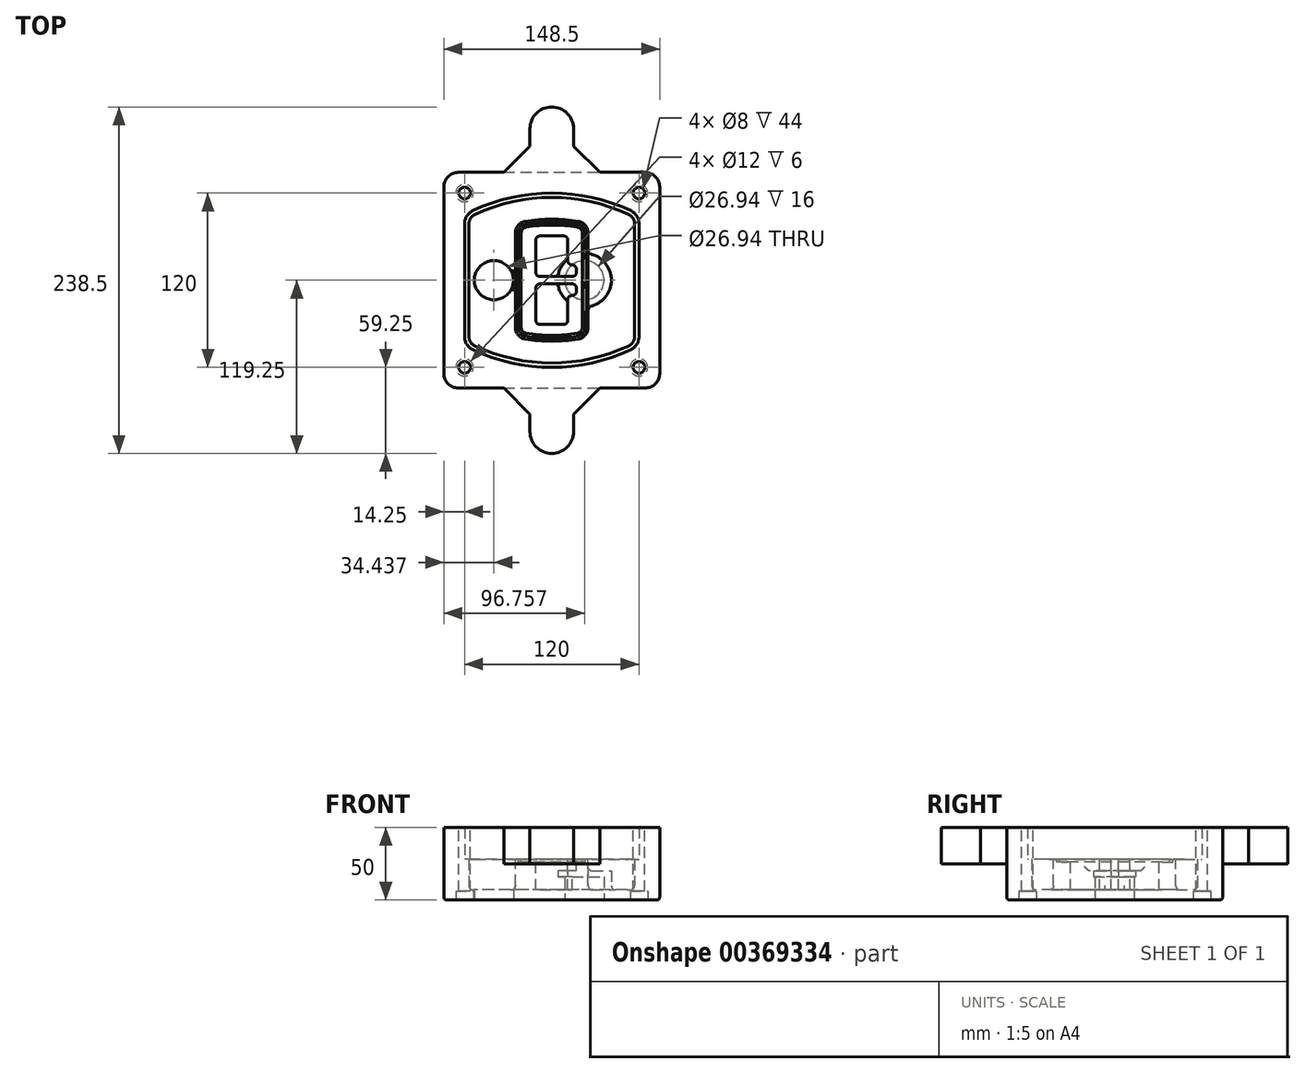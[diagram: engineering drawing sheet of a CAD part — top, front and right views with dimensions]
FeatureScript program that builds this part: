
annotation { "Feature Type Name" : "Feature", "Feature Type Description" : "" }
export const myFeature = defineFeature(function(context is Context, id is Id, definition is map)
    precondition{}
    {
        {
            var Q0;
            Q0=qCreatedBy(makeId("Top.planeOp"),FACE);
            var sketch = newSketch(context, id + "F0", { "sketchPlane" : qUnion([Q0])});
            skPoint(sketch, "E0.rect.middle", {"position": v(0, 0) * mm});
            skLineSegment(sketch, "E1.bottom", {"start": v(-64.25, -74.25) * mm, "end": v(64.25, -74.25) * mm});
            skLineSegment(sketch, "E1.top", {"start": v(-64.25, 74.25) * mm, "end": v(64.25, 74.25) * mm});
            skLineSegment(sketch, "E1.left", {"start": v(-74.25, -64.25) * mm, "end": v(-74.25, 64.25) * mm});
            skLineSegment(sketch, "E1.right", {"start": v(74.25, -64.25) * mm, "end": v(74.25, 64.25) * mm});
            skLineSegment(sketch, "E2", {"start": v(-74.25, 74.25) * mm, "end": v(74.25, -74.25) * mm, "construction": true});
            skLineSegment(sketch, "E3", {"start": v(74.25, 74.25) * mm, "end": v(-74.25, -74.25) * mm, "construction": true});
            skCircle(sketch, "E4", {"center": v(-60, 60) * mm, "radius": 4 * mm});
            skCircle(sketch, "E5", {"center": v(60, 60) * mm, "radius": 4 * mm});
            skCircle(sketch, "E6", {"center": v(60, -60) * mm, "radius": 4 * mm});
            skCircle(sketch, "E7", {"center": v(-60, -60) * mm, "radius": 4 * mm});
            skLineSegment(sketch, "E8", {"start": v(-60, 60) * mm, "end": v(60, 60) * mm, "construction": true});
            skLineSegment(sketch, "E9", {"start": v(60, 60) * mm, "end": v(60, -60) * mm, "construction": true});
            skLineSegment(sketch, "E10", {"start": v(60, -60) * mm, "end": v(-60, -60) * mm, "construction": true});
            skLineSegment(sketch, "E11", {"start": v(-60, -60) * mm, "end": v(-60, 60) * mm, "construction": true});
            skLineSegment(sketch, "E12", {"start": v(-60, 38.83) * mm, "end": v(-60, -38.83) * mm});
            skLineSegment(sketch, "E13", {"start": v(60, 38.83) * mm, "end": v(60, -38.83) * mm});
            skArc(sketch, "E14", {"start": v(54.26, 47.88) * mm, "mid": v(0, 60) * mm, "end": v(-54.26, 47.88) * mm});
            skArc(sketch, "E15", {"start": v(-54.26, -47.88) * mm, "mid": v(0, -60) * mm, "end": v(54.26, -47.88) * mm});
            skLineSegment(sketch, "E16", {"start": v(-60, 0) * mm, "end": v(60, 0) * mm, "construction": true});
            skPoint(sketch, "E17.visualSharp", {"position": v(-60, -45) * mm});
            skArc(sketch, "E17.filletArc", {"start": v(-60, -38.83) * mm, "mid": v(-58.44, -44.2) * mm, "end": v(-54.26, -47.88) * mm});
            skPoint(sketch, "E18.visualSharp", {"position": v(-60, 45) * mm});
            skArc(sketch, "E18.filletArc", {"start": v(-54.26, 47.88) * mm, "mid": v(-58.44, 44.2) * mm, "end": v(-60, 38.83) * mm});
            skPoint(sketch, "E19.visualSharp", {"position": v(60, 45) * mm});
            skArc(sketch, "E19.filletArc", {"start": v(60, 38.83) * mm, "mid": v(58.44, 44.2) * mm, "end": v(54.26, 47.88) * mm});
            skPoint(sketch, "E20.visualSharp", {"position": v(60, -45) * mm});
            skArc(sketch, "E20.filletArc", {"start": v(54.26, -47.88) * mm, "mid": v(58.44, -44.2) * mm, "end": v(60, -38.83) * mm});
            skPoint(sketch, "E21.visualSharp", {"position": v(-74.25, 74.25) * mm});
            skArc(sketch, "E21.filletArc", {"start": v(-64.25, 74.25) * mm, "mid": v(-71.32, 71.32) * mm, "end": v(-74.25, 64.25) * mm});
            skPoint(sketch, "E22.visualSharp", {"position": v(74.25, 74.25) * mm});
            skArc(sketch, "E22.filletArc", {"start": v(74.25, 64.25) * mm, "mid": v(71.32, 71.32) * mm, "end": v(64.25, 74.25) * mm});
            skPoint(sketch, "E23.visualSharp", {"position": v(74.25, -74.25) * mm});
            skArc(sketch, "E23.filletArc", {"start": v(64.25, -74.25) * mm, "mid": v(71.32, -71.32) * mm, "end": v(74.25, -64.25) * mm});
            skPoint(sketch, "E24.visualSharp", {"position": v(-74.25, -74.25) * mm});
            skArc(sketch, "E24.filletArc", {"start": v(-74.25, -64.25) * mm, "mid": v(-71.32, -71.32) * mm, "end": v(-64.25, -74.25) * mm});
            skArc(sketch, "E25.0", {"start": v(57, 38.83) * mm, "mid": v(55.9, 42.58) * mm, "end": v(52.98, 45.17) * mm});
            skLineSegment(sketch, "E25.1", {"start": v(57, 38.83) * mm, "end": v(57, -38.83) * mm});
            skArc(sketch, "E25.2", {"start": v(52.98, -45.17) * mm, "mid": v(55.9, -42.58) * mm, "end": v(57, -38.83) * mm});
            skArc(sketch, "E25.3", {"start": v(-52.98, -45.17) * mm, "mid": v(0, -57) * mm, "end": v(52.98, -45.17) * mm});
            skArc(sketch, "E25.4", {"start": v(-57, -38.83) * mm, "mid": v(-55.9, -42.58) * mm, "end": v(-52.98, -45.17) * mm});
            skArc(sketch, "E25.5", {"start": v(52.98, 45.17) * mm, "mid": v(0, 57) * mm, "end": v(-52.98, 45.17) * mm});
            skLineSegment(sketch, "E25.6", {"start": v(-57, 38.83) * mm, "end": v(-57, -38.83) * mm});
            skArc(sketch, "E25.7", {"start": v(-52.98, 45.17) * mm, "mid": v(-55.9, 42.58) * mm, "end": v(-57, 38.83) * mm});
            skArc(sketch, "E26.0", {"start": v(-55.96, 51.5) * mm, "mid": v(-61.82, 46.33) * mm, "end": v(-64, 38.83) * mm});
            skArc(sketch, "E26.1", {"start": v(55.96, 51.5) * mm, "mid": v(0, 64) * mm, "end": v(-55.96, 51.5) * mm});
            skArc(sketch, "E26.2", {"start": v(64, 38.83) * mm, "mid": v(61.82, 46.33) * mm, "end": v(55.96, 51.5) * mm});
            skLineSegment(sketch, "E26.3", {"start": v(64, 38.83) * mm, "end": v(64, -38.83) * mm});
            skArc(sketch, "E26.4", {"start": v(55.96, -51.5) * mm, "mid": v(61.82, -46.33) * mm, "end": v(64, -38.83) * mm});
            skLineSegment(sketch, "E26.5", {"start": v(-64, 38.83) * mm, "end": v(-64, -38.83) * mm});
            skArc(sketch, "E26.6", {"start": v(-55.96, -51.5) * mm, "mid": v(0, -64) * mm, "end": v(55.96, -51.5) * mm});
            skArc(sketch, "E26.7", {"start": v(-64, -38.83) * mm, "mid": v(-61.82, -46.33) * mm, "end": v(-55.96, -51.5) * mm});
            skSolve(sketch);
        }
        {
            var Q0;
            Q0=makeQuery(id+"F0.imprint","IMPRINT",FACE,{"disambiguationData":[TD([[makeQuery(id+"F0.imprint","IMPRINT",EDGE,{"derivedFrom":sQuery(id+"F0.wireOp",EDGE,"E1.bottom")}),1.0]])]});
            var Q1;
            Q1=makeQuery(id+"F0.imprint","IMPRINT",FACE,{"disambiguationData":[TD([[makeQuery(id+"F0.imprint","IMPRINT",EDGE,{"derivedFrom":sQuery(id+"F0.wireOp",EDGE,"E12")}),1.0]])]});
            var Q2;
            Q2=makeQuery(id+"F0.imprint","IMPRINT",FACE,{"disambiguationData":[TD([[makeQuery(id+"F0.imprint","IMPRINT",EDGE,{"derivedFrom":sQuery(id+"F0.wireOp",EDGE,"E25.0")}),1.0]])]});
            var Q3;
            Q3=makeQuery(id+"F0.imprint","IMPRINT",FACE,{"disambiguationData":[TD([[makeQuery(id+"F0.imprint","IMPRINT",EDGE,{"derivedFrom":sQuery(id+"F0.wireOp",EDGE,"E12")}),-1.0]])]});
            extrude(context, id + "F1", {"entities" : qUnion([Q0, Q1, Q2, Q3]), "oppositeDirection" : true, "depth" : 25 * mm});
        }
        {
            var Q0;
            Q0=makeQuery(id+"F0.imprint","IMPRINT",FACE,{"disambiguationData":[TD([[makeQuery(id+"F0.imprint","IMPRINT",EDGE,{"derivedFrom":sQuery(id+"F0.wireOp",EDGE,"E12")}),1.0]])]});
            extrude(context, id + "F2", {"entities" : qUnion([Q0]), "operationType" : NewBodyOperationType.ADD, "depth" : 3 * mm});
        }
        {
            var Q0;
            Q0=makeQuery(id+"F0.imprint","IMPRINT",FACE,{"disambiguationData":[TD([[makeQuery(id+"F0.imprint","IMPRINT",EDGE,{"derivedFrom":sQuery(id+"F0.wireOp",EDGE,"E25.0")}),1.0]])]});
            extrude(context, id + "F3", {"entities" : qUnion([Q0]), "operationType" : NewBodyOperationType.REMOVE, "oppositeDirection" : true, "depth" : 18 * mm});
        }
        {
            var Q0;
            Q0=makeQuery(id+"F2.opExtrude","CAP_FACE",FACE,{"disambiguationData":[OSD([sQuery(id+"F0.wireOp",EDGE,"E12"),sQuery(id+"F0.wireOp",EDGE,"E13"),sQuery(id+"F0.wireOp",EDGE,"E14"),sQuery(id+"F0.wireOp",EDGE,"E15"),sQuery(id+"F0.wireOp",EDGE,"E17.filletArc"),sQuery(id+"F0.wireOp",EDGE,"E18.filletArc"),sQuery(id+"F0.wireOp",EDGE,"E19.filletArc"),sQuery(id+"F0.wireOp",EDGE,"E20.filletArc"),sQuery(id+"F0.wireOp",EDGE,"E25.0"),sQuery(id+"F0.wireOp",EDGE,"E25.1"),sQuery(id+"F0.wireOp",EDGE,"E25.2"),sQuery(id+"F0.wireOp",EDGE,"E25.3"),sQuery(id+"F0.wireOp",EDGE,"E25.4"),sQuery(id+"F0.wireOp",EDGE,"E25.5"),sQuery(id+"F0.wireOp",EDGE,"E25.6"),sQuery(id+"F0.wireOp",EDGE,"E25.7")])],"isStart":false});
            var sketch = newSketch(context, id + "F4", { "sketchPlane" : qUnion([Q0])});
            skArc(sketch, "E27.0", {"start": v(-18.34, -40.45) * mm, "mid": v(0, -42) * mm, "end": v(18.34, -40.45) * mm});
            skArc(sketch, "E28.0", {"start": v(18.34, 40.45) * mm, "mid": v(0, 42) * mm, "end": v(-18.34, 40.45) * mm});
            skLineSegment(sketch, "E29", {"start": v(-25, 32.57) * mm, "end": v(-25, -32.57) * mm});
            skLineSegment(sketch, "E30", {"start": v(25, 32.57) * mm, "end": v(25, -32.57) * mm});
            skLineSegment(sketch, "E31", {"start": v(-25, 39.1) * mm, "end": v(25, 39.1) * mm, "construction": true});
            skLineSegment(sketch, "E32", {"start": v(-25, -39.1) * mm, "end": v(25, -39.1) * mm, "construction": true});
            skPoint(sketch, "E33.visualSharp", {"position": v(-25, 39.1) * mm});
            skArc(sketch, "E33.filletArc", {"start": v(-18.34, 40.45) * mm, "mid": v(-23.11, 37.73) * mm, "end": v(-25, 32.57) * mm});
            skPoint(sketch, "E34.visualSharp", {"position": v(25, 39.1) * mm});
            skArc(sketch, "E34.filletArc", {"start": v(25, 32.57) * mm, "mid": v(23.11, 37.73) * mm, "end": v(18.34, 40.45) * mm});
            skPoint(sketch, "E35.visualSharp", {"position": v(25, -39.1) * mm});
            skArc(sketch, "E35.filletArc", {"start": v(18.34, -40.45) * mm, "mid": v(23.11, -37.73) * mm, "end": v(25, -32.57) * mm});
            skPoint(sketch, "E36.visualSharp", {"position": v(-25, -39.1) * mm});
            skArc(sketch, "E36.filletArc", {"start": v(-25, -32.57) * mm, "mid": v(-23.11, -37.73) * mm, "end": v(-18.34, -40.45) * mm});
            skArc(sketch, "E37.0", {"start": v(52.98, 45.17) * mm, "mid": v(0, 57) * mm, "end": v(-52.98, 45.17) * mm});
            skArc(sketch, "E37.1", {"start": v(-52.98, 45.17) * mm, "mid": v(-55.9, 42.58) * mm, "end": v(-57, 38.83) * mm});
            skLineSegment(sketch, "E37.2", {"start": v(-57, 38.83) * mm, "end": v(-57, -38.83) * mm});
            skArc(sketch, "E37.3", {"start": v(-57, -38.83) * mm, "mid": v(-55.9, -42.58) * mm, "end": v(-52.98, -45.17) * mm});
            skArc(sketch, "E37.4", {"start": v(-52.98, -45.17) * mm, "mid": v(0, -57) * mm, "end": v(52.98, -45.17) * mm});
            skArc(sketch, "E37.5", {"start": v(52.98, -45.17) * mm, "mid": v(55.9, -42.58) * mm, "end": v(57, -38.83) * mm});
            skLineSegment(sketch, "E37.6", {"start": v(57, 38.83) * mm, "end": v(57, -38.83) * mm});
            skArc(sketch, "E37.7", {"start": v(57, 38.83) * mm, "mid": v(55.9, 42.58) * mm, "end": v(52.98, 45.17) * mm});
            skLineSegment(sketch, "E38.0", {"start": v(23, 32.57) * mm, "end": v(23, -32.57) * mm});
            skArc(sketch, "E38.1", {"start": v(18, -38.48) * mm, "mid": v(21.58, -36.44) * mm, "end": v(23, -32.57) * mm});
            skArc(sketch, "E38.2", {"start": v(-18, -38.48) * mm, "mid": v(0, -40) * mm, "end": v(18, -38.48) * mm});
            skArc(sketch, "E38.3", {"start": v(-23, -32.57) * mm, "mid": v(-21.58, -36.44) * mm, "end": v(-18, -38.48) * mm});
            skLineSegment(sketch, "E38.4", {"start": v(-23, 32.57) * mm, "end": v(-23, -32.57) * mm});
            skArc(sketch, "E38.5", {"start": v(23, 32.57) * mm, "mid": v(21.58, 36.44) * mm, "end": v(18, 38.48) * mm});
            skArc(sketch, "E38.6", {"start": v(-18, 38.48) * mm, "mid": v(-21.58, 36.44) * mm, "end": v(-23, 32.57) * mm});
            skArc(sketch, "E38.7", {"start": v(18, 38.48) * mm, "mid": v(0, 40) * mm, "end": v(-18, 38.48) * mm});
            skArc(sketch, "E39.0", {"start": v(21, 32.57) * mm, "mid": v(20.06, 35.15) * mm, "end": v(17.67, 36.5) * mm});
            skLineSegment(sketch, "E39.1", {"start": v(21, 32.57) * mm, "end": v(21, -32.57) * mm});
            skArc(sketch, "E39.2", {"start": v(17.67, -36.5) * mm, "mid": v(20.06, -35.15) * mm, "end": v(21, -32.57) * mm});
            skArc(sketch, "E39.3", {"start": v(-17.67, -36.5) * mm, "mid": v(0, -38) * mm, "end": v(17.67, -36.5) * mm});
            skArc(sketch, "E39.4", {"start": v(-21, -32.57) * mm, "mid": v(-20.06, -35.15) * mm, "end": v(-17.67, -36.5) * mm});
            skArc(sketch, "E39.5", {"start": v(17.67, 36.5) * mm, "mid": v(0, 38) * mm, "end": v(-17.67, 36.5) * mm});
            skLineSegment(sketch, "E39.6", {"start": v(-21, 32.57) * mm, "end": v(-21, -32.57) * mm});
            skArc(sketch, "E39.7", {"start": v(-17.67, 36.5) * mm, "mid": v(-20.06, 35.15) * mm, "end": v(-21, 32.57) * mm});
            skLineSegment(sketch, "E40", {"start": v(-25, 0) * mm, "end": v(25, 0) * mm, "construction": true});
            skLineSegment(sketch, "E41", {"start": v(-11, 5.5) * mm, "end": v(-11, 27.5) * mm});
            skLineSegment(sketch, "E42", {"start": v(-8, 30.5) * mm, "end": v(8, 30.5) * mm});
            skLineSegment(sketch, "E43", {"start": v(11, 27.5) * mm, "end": v(11, 13.5) * mm});
            skLineSegment(sketch, "E44", {"start": v(14, 10.5) * mm, "end": v(14, 10.5) * mm});
            skLineSegment(sketch, "E45", {"start": v(17, 7.5) * mm, "end": v(17, 5.5) * mm});
            skLineSegment(sketch, "E46", {"start": v(14, 2.5) * mm, "end": v(-8, 2.5) * mm});
            skPoint(sketch, "E47.visualSharp", {"position": v(-11, 30.5) * mm});
            skArc(sketch, "E47.filletArc", {"start": v(-8, 30.5) * mm, "mid": v(-10.12, 29.62) * mm, "end": v(-11, 27.5) * mm});
            skPoint(sketch, "E48.visualSharp", {"position": v(11, 30.5) * mm});
            skArc(sketch, "E48.filletArc", {"start": v(11, 27.5) * mm, "mid": v(10.12, 29.62) * mm, "end": v(8, 30.5) * mm});
            skPoint(sketch, "E49.visualSharp", {"position": v(11, 10.5) * mm});
            skArc(sketch, "E49.filletArc", {"start": v(11, 13.5) * mm, "mid": v(11.88, 11.38) * mm, "end": v(14, 10.5) * mm});
            skPoint(sketch, "E50.visualSharp", {"position": v(17, 10.5) * mm});
            skArc(sketch, "E50.filletArc", {"start": v(17, 7.5) * mm, "mid": v(16.12, 9.62) * mm, "end": v(14, 10.5) * mm});
            skPoint(sketch, "E51.visualSharp", {"position": v(17, 2.5) * mm});
            skArc(sketch, "E51.filletArc", {"start": v(14, 2.5) * mm, "mid": v(16.12, 3.38) * mm, "end": v(17, 5.5) * mm});
            skPoint(sketch, "E52.visualSharp", {"position": v(-11, 2.5) * mm});
            skArc(sketch, "E52.filletArc", {"start": v(-11, 5.5) * mm, "mid": v(-10.12, 3.38) * mm, "end": v(-8, 2.5) * mm});
            skLineSegment(sketch, "E53.0.MirrorCS", {"start": v(14, -2.5) * mm, "end": v(-8, -2.5) * mm});
            skArc(sketch, "E54.0.MirrorCS", {"start": v(-11, -5.5) * mm, "mid": v(-10.12, -3.38) * mm, "end": v(-8, -2.5) * mm});
            skLineSegment(sketch, "E55.0.MirrorCS", {"start": v(-11, -5.5) * mm, "end": v(-11, -27.5) * mm});
            skArc(sketch, "E56.0.MirrorCS", {"start": v(-8, -30.5) * mm, "mid": v(-10.12, -29.62) * mm, "end": v(-11, -27.5) * mm});
            skLineSegment(sketch, "E57.0.MirrorCS", {"start": v(-8, -30.5) * mm, "end": v(8, -30.5) * mm});
            skArc(sketch, "E58.0.MirrorCS", {"start": v(11, -27.5) * mm, "mid": v(10.12, -29.62) * mm, "end": v(8, -30.5) * mm});
            skLineSegment(sketch, "E59.0.MirrorCS", {"start": v(11, -27.5) * mm, "end": v(11, -13.5) * mm});
            skArc(sketch, "E60.0.MirrorCS", {"start": v(11, -13.5) * mm, "mid": v(11.88, -11.38) * mm, "end": v(14, -10.5) * mm});
            skArc(sketch, "E61.0.MirrorCS", {"start": v(17, -7.5) * mm, "mid": v(16.12, -9.62) * mm, "end": v(14, -10.5) * mm});
            skLineSegment(sketch, "E62.0.MirrorCS", {"start": v(17, -7.5) * mm, "end": v(17, -5.5) * mm});
            skArc(sketch, "E63.0.MirrorCS", {"start": v(14, -2.5) * mm, "mid": v(16.12, -3.38) * mm, "end": v(17, -5.5) * mm});
            skSolve(sketch);
        }
        {
            var Q0;
            Q0=makeQuery(id+"F4.imprint","IMPRINT",FACE,{"disambiguationData":[TD([[makeQuery(id+"F4.imprint","IMPRINT",EDGE,{"derivedFrom":sQuery(id+"F4.wireOp",EDGE,"E27.0")}),1.0]])]});
            var Q1;
            Q1=makeQuery(id+"F4.imprint","IMPRINT",FACE,{"disambiguationData":[TD([[makeQuery(id+"F4.imprint","IMPRINT",EDGE,{"derivedFrom":sQuery(id+"F4.wireOp",EDGE,"E38.0")}),-1.0]])]});
            var Q2;
            Q2=makeQuery(id+"F4.imprint","IMPRINT",FACE,{"disambiguationData":[TD([[makeQuery(id+"F4.imprint","IMPRINT",EDGE,{"derivedFrom":sQuery(id+"F4.wireOp",EDGE,"E39.0")}),1.0]])]});
            extrude(context, id + "F5", {"entities" : qUnion([Q0, Q1, Q2]), "operationType" : NewBodyOperationType.ADD, "endBound" : BoundingType.UP_TO_NEXT, "oppositeDirection" : true, "depth" : 25 * mm});
        }
        {
            var Q0;
            Q0=makeQuery(id+"F4.imprint","IMPRINT",FACE,{"disambiguationData":[TD([[makeQuery(id+"F4.imprint","IMPRINT",EDGE,{"derivedFrom":sQuery(id+"F4.wireOp",EDGE,"E38.0")}),-1.0]])]});
            extrude(context, id + "F6", {"entities" : qUnion([Q0]), "operationType" : NewBodyOperationType.REMOVE, "oppositeDirection" : true, "depth" : 2 * mm});
        }
        {
            var Q0;
            Q0=makeQuery(id+"F1.opExtrude","CAP_FACE",FACE,{"disambiguationData":[OSD([sQuery(id+"F0.wireOp",EDGE,"E1.bottom"),sQuery(id+"F0.wireOp",EDGE,"E1.top"),sQuery(id+"F0.wireOp",EDGE,"E1.left"),sQuery(id+"F0.wireOp",EDGE,"E1.right"),sQuery(id+"F0.wireOp",EDGE,"E4"),sQuery(id+"F0.wireOp",EDGE,"E5"),sQuery(id+"F0.wireOp",EDGE,"E6"),sQuery(id+"F0.wireOp",EDGE,"E7"),sQuery(id+"F0.wireOp",EDGE,"E21.filletArc"),sQuery(id+"F0.wireOp",EDGE,"E22.filletArc"),sQuery(id+"F0.wireOp",EDGE,"E23.filletArc"),sQuery(id+"F0.wireOp",EDGE,"E24.filletArc")])],"isStart":false});
            var sketch = newSketch(context, id + "F7", { "sketchPlane" : qUnion([Q0])});
            skCircle(sketch, "E64", {"center": v(22.5, 0) * mm, "radius": 13.47 * mm});
            skCircle(sketch, "E65", {"center": v(-39.81, 0) * mm, "radius": 13.47 * mm});
            skLineSegment(sketch, "E66", {"start": v(74.25, 0) * mm, "end": v(-74.25, 0) * mm});
            skCircle(sketch, "E67", {"center": v(22.5, 0) * mm, "radius": 18.47 * mm});
            skCircle(sketch, "E68", {"center": v(60, -60) * mm, "radius": 6 * mm});
            skCircle(sketch, "E69", {"center": v(-60, -60) * mm, "radius": 6 * mm});
            skCircle(sketch, "E70", {"center": v(-60, 60) * mm, "radius": 6 * mm});
            skCircle(sketch, "E71", {"center": v(60, 60) * mm, "radius": 6 * mm});
            skSolve(sketch);
        }
        {
            var Q0;
            {var subQ1=sQuery(id+"F7.wireOp",EDGE,"E66");var subQ4=sQuery(id+"F7.wireOp",EDGE,"E64");var subQ6=makeQuery(id+"F7.imprint","INTERSECT",VERTEX,{"disambiguationData":[OD(0.0)],"derivedFrom":[subQ4,subQ1]});Q0=makeQuery(id+"F7.imprint","IMPRINT",FACE,{"disambiguationData":[TD([[makeQuery(id+"F7.imprint","IMPRINT",EDGE,{"disambiguationData":[TD([[subQ6,-1.0]])],"derivedFrom":subQ4}),-1.0]])]});}
            var Q1;
            {var subQ0=sQuery(id+"F7.wireOp",EDGE,"E66");var subQ1=sQuery(id+"F7.wireOp",EDGE,"E64");var subQ3=makeQuery(id+"F7.imprint","INTERSECT",VERTEX,{"disambiguationData":[OD(0.0)],"derivedFrom":[subQ1,subQ0]});Q1=makeQuery(id+"F7.imprint","IMPRINT",FACE,{"disambiguationData":[TD([[makeQuery(id+"F7.imprint","IMPRINT",EDGE,{"disambiguationData":[TD([[subQ3,-1.0]])],"derivedFrom":subQ1}),1.0]])]});}
            var Q2;
            {var subQ0=sQuery(id+"F7.wireOp",EDGE,"E66");var subQ1=sQuery(id+"F7.wireOp",EDGE,"E64");var subQ3=makeQuery(id+"F7.imprint","INTERSECT",VERTEX,{"disambiguationData":[OD(0.0)],"derivedFrom":[subQ1,subQ0]});Q2=makeQuery(id+"F7.imprint","IMPRINT",FACE,{"disambiguationData":[TD([[makeQuery(id+"F7.imprint","IMPRINT",EDGE,{"disambiguationData":[TD([[subQ3,1.0]])],"derivedFrom":subQ1}),1.0]])]});}
            var Q3;
            {var subQ1=sQuery(id+"F7.wireOp",EDGE,"E66");var subQ4=sQuery(id+"F7.wireOp",EDGE,"E64");var subQ6=makeQuery(id+"F7.imprint","INTERSECT",VERTEX,{"disambiguationData":[OD(0.0)],"derivedFrom":[subQ4,subQ1]});Q3=makeQuery(id+"F7.imprint","IMPRINT",FACE,{"disambiguationData":[TD([[makeQuery(id+"F7.imprint","IMPRINT",EDGE,{"disambiguationData":[TD([[subQ6,1.0]])],"derivedFrom":subQ4}),-1.0]])]});}
            extrude(context, id + "F8", {"entities" : qUnion([Q0, Q1, Q2, Q3]), "operationType" : NewBodyOperationType.ADD, "oppositeDirection" : true, "depth" : 20 * mm});
        }
        {
            var Q0;
            {var subQ0=sQuery(id+"F7.wireOp",EDGE,"E66");var subQ1=sQuery(id+"F7.wireOp",EDGE,"E64");var subQ3=makeQuery(id+"F7.imprint","INTERSECT",VERTEX,{"disambiguationData":[OD(0.0)],"derivedFrom":[subQ1,subQ0]});Q0=makeQuery(id+"F7.imprint","IMPRINT",FACE,{"disambiguationData":[TD([[makeQuery(id+"F7.imprint","IMPRINT",EDGE,{"disambiguationData":[TD([[subQ3,-1.0]])],"derivedFrom":subQ1}),1.0]])]});}
            var Q1;
            {var subQ0=sQuery(id+"F7.wireOp",EDGE,"E66");var subQ1=sQuery(id+"F7.wireOp",EDGE,"E64");var subQ3=makeQuery(id+"F7.imprint","INTERSECT",VERTEX,{"disambiguationData":[OD(0.0)],"derivedFrom":[subQ1,subQ0]});Q1=makeQuery(id+"F7.imprint","IMPRINT",FACE,{"disambiguationData":[TD([[makeQuery(id+"F7.imprint","IMPRINT",EDGE,{"disambiguationData":[TD([[subQ3,1.0]])],"derivedFrom":subQ1}),1.0]])]});}
            extrude(context, id + "F9", {"entities" : qUnion([Q0, Q1]), "operationType" : NewBodyOperationType.REMOVE, "oppositeDirection" : true, "depth" : 16 * mm});
        }
        {
            var Q0;
            {var subQ0=sQuery(id+"F7.wireOp",EDGE,"E66");var subQ1=sQuery(id+"F7.wireOp",EDGE,"E65");var subQ3=makeQuery(id+"F7.imprint","INTERSECT",VERTEX,{"disambiguationData":[OD(0.0)],"derivedFrom":[subQ1,subQ0]});Q0=makeQuery(id+"F7.imprint","IMPRINT",FACE,{"disambiguationData":[TD([[makeQuery(id+"F7.imprint","IMPRINT",EDGE,{"disambiguationData":[TD([[subQ3,-1.0]])],"derivedFrom":subQ1}),1.0]])]});}
            var Q1;
            {var subQ0=sQuery(id+"F7.wireOp",EDGE,"E66");var subQ1=sQuery(id+"F7.wireOp",EDGE,"E65");var subQ3=makeQuery(id+"F7.imprint","INTERSECT",VERTEX,{"disambiguationData":[OD(0.0)],"derivedFrom":[subQ1,subQ0]});Q1=makeQuery(id+"F7.imprint","IMPRINT",FACE,{"disambiguationData":[TD([[makeQuery(id+"F7.imprint","IMPRINT",EDGE,{"disambiguationData":[TD([[subQ3,1.0]])],"derivedFrom":subQ1}),1.0]])]});}
            extrude(context, id + "F10", {"entities" : qUnion([Q0, Q1]), "operationType" : NewBodyOperationType.REMOVE, "oppositeDirection" : true, "depth" : 25 * mm});
        }
        {
            var Q0;
            Q0=makeQuery(id+"F7.imprint","IMPRINT",FACE,{"disambiguationData":[TD([[makeQuery(id+"F7.imprint","IMPRINT",EDGE,{"derivedFrom":sQuery(id+"F7.wireOp",EDGE,"E68")}),1.0]])]});
            var Q1;
            Q1=makeQuery(id+"F7.imprint","IMPRINT",FACE,{"disambiguationData":[TD([[makeQuery(id+"F7.imprint","IMPRINT",EDGE,{"derivedFrom":makeQuery(id+"F1.opExtrude","CAP_EDGE",EDGE,{"disambiguationData":[OSD([sQuery(id+"F0.wireOp",EDGE,"E5")])],"isStart":false})}),-1.0]])]});
            var Q2;
            Q2=makeQuery(id+"F7.imprint","IMPRINT",FACE,{"disambiguationData":[TD([[makeQuery(id+"F7.imprint","IMPRINT",EDGE,{"derivedFrom":sQuery(id+"F7.wireOp",EDGE,"E69")}),1.0]])]});
            var Q3;
            Q3=makeQuery(id+"F7.imprint","IMPRINT",FACE,{"disambiguationData":[TD([[makeQuery(id+"F7.imprint","IMPRINT",EDGE,{"derivedFrom":makeQuery(id+"F1.opExtrude","CAP_EDGE",EDGE,{"disambiguationData":[OSD([sQuery(id+"F0.wireOp",EDGE,"E4")])],"isStart":false})}),-1.0]])]});
            var Q4;
            Q4=makeQuery(id+"F7.imprint","IMPRINT",FACE,{"disambiguationData":[TD([[makeQuery(id+"F7.imprint","IMPRINT",EDGE,{"derivedFrom":sQuery(id+"F7.wireOp",EDGE,"E70")}),1.0]])]});
            var Q5;
            Q5=makeQuery(id+"F7.imprint","IMPRINT",FACE,{"disambiguationData":[TD([[makeQuery(id+"F7.imprint","IMPRINT",EDGE,{"derivedFrom":makeQuery(id+"F1.opExtrude","CAP_EDGE",EDGE,{"disambiguationData":[OSD([sQuery(id+"F0.wireOp",EDGE,"E7")])],"isStart":false})}),-1.0]])]});
            var Q6;
            Q6=makeQuery(id+"F7.imprint","IMPRINT",FACE,{"disambiguationData":[TD([[makeQuery(id+"F7.imprint","IMPRINT",EDGE,{"derivedFrom":sQuery(id+"F7.wireOp",EDGE,"E71")}),1.0]])]});
            var Q7;
            Q7=makeQuery(id+"F7.imprint","IMPRINT",FACE,{"disambiguationData":[TD([[makeQuery(id+"F7.imprint","IMPRINT",EDGE,{"derivedFrom":makeQuery(id+"F1.opExtrude","CAP_EDGE",EDGE,{"disambiguationData":[OSD([sQuery(id+"F0.wireOp",EDGE,"E6")])],"isStart":false})}),-1.0]])]});
            extrude(context, id + "F11", {"entities" : qUnion([Q0, Q1, Q2, Q3, Q4, Q5, Q6, Q7]), "operationType" : NewBodyOperationType.REMOVE, "oppositeDirection" : true, "depth" : 6 * mm});
        }
        {
            var Q0;
            Q0=makeQuery(id+"F9.boolean.opBoolean","COPY",FACE,{"derivedFrom":makeQuery(id+"F9.opExtrude","CAP_FACE",FACE,{"disambiguationData":[OSD([sQuery(id+"F7.wireOp",EDGE,"E64")])],"isStart":false})});
            var sketch = newSketch(context, id + "F12", { "sketchPlane" : qUnion([Q0])});
            skArc(sketch, "E72.0", {"start": v(11, 14.45) * mm, "mid": v(6.45, 9.13) * mm, "end": v(4.2, 2.5) * mm});
            skArc(sketch, "E72.1", {"start": v(4.2, -2.5) * mm, "mid": v(6.45, -9.13) * mm, "end": v(11, -14.45) * mm});
            skLineSegment(sketch, "E73", {"start": v(4.2, -2.5) * mm, "end": v(14, -2.5) * mm});
            skLineSegment(sketch, "E74.0", {"start": v(14, 2.5) * mm, "end": v(4.2, 2.5) * mm});
            skArc(sketch, "E74.1", {"start": v(14, 2.5) * mm, "mid": v(16.12, 3.38) * mm, "end": v(17, 5.5) * mm});
            skLineSegment(sketch, "E74.2", {"start": v(17, 7.5) * mm, "end": v(17, 5.5) * mm});
            skArc(sketch, "E74.3", {"start": v(17, 7.5) * mm, "mid": v(16.12, 9.62) * mm, "end": v(14, 10.5) * mm});
            skArc(sketch, "E74.4", {"start": v(11, 13.5) * mm, "mid": v(11.88, 11.38) * mm, "end": v(14, 10.5) * mm});
            skLineSegment(sketch, "E74.5", {"start": v(11, 14.45) * mm, "end": v(11, 13.5) * mm});
            skLineSegment(sketch, "E74.7", {"start": v(14, -2.5) * mm, "end": v(4.2, -2.5) * mm});
            skArc(sketch, "E74.8", {"start": v(14, -2.5) * mm, "mid": v(16.12, -3.38) * mm, "end": v(17, -5.5) * mm});
            skLineSegment(sketch, "E74.9", {"start": v(17, -7.5) * mm, "end": v(17, -5.5) * mm});
            skArc(sketch, "E74.10", {"start": v(17, -7.5) * mm, "mid": v(16.12, -9.62) * mm, "end": v(14, -10.5) * mm});
            skArc(sketch, "E74.11", {"start": v(11, -13.5) * mm, "mid": v(11.88, -11.38) * mm, "end": v(14, -10.5) * mm});
            skLineSegment(sketch, "E74.12", {"start": v(11, -14.45) * mm, "end": v(11, -13.5) * mm});
            skPoint(sketch, "E75.orphan", {"position": v(11, -27.5) * mm});
            skPoint(sketch, "E76.orphan", {"position": v(-8, -2.5) * mm});
            skPoint(sketch, "E77.orphan", {"position": v(-8, 2.5) * mm});
            skPoint(sketch, "E78.orphan", {"position": v(11, 27.5) * mm});
            skSolve(sketch);
        }
        {
            var Q0;
            {var subQ7=sQuery(id+"F12.wireOp",EDGE,"E72.0");var subQ14=sQuery(id+"F12.wireOp",EDGE,"E72.1");var subQ16=sQuery(id+"F12.wireOp",EDGE,"E74.1");var subQ18=sQuery(id+"F12.wireOp",EDGE,"E74.8");Q0=qUnion([makeQuery(id+"F12.imprint","IMPRINT",FACE,{"disambiguationData":[TD([[makeQuery(id+"F12.imprint","IMPRINT",EDGE,{"derivedFrom":subQ7}),1.0]])]}),makeQuery(id+"F12.imprint","IMPRINT",FACE,{"disambiguationData":[TD([[makeQuery(id+"F12.imprint","IMPRINT",EDGE,{"derivedFrom":subQ14}),1.0]])]}),makeQuery(id+"F12.imprint","IMPRINT",FACE,{"disambiguationData":[TD([[makeQuery(id+"F12.imprint","IMPRINT",EDGE,{"derivedFrom":subQ16}),1.0]])]}),makeQuery(id+"F12.imprint","IMPRINT",FACE,{"disambiguationData":[TD([[makeQuery(id+"F12.imprint","IMPRINT",EDGE,{"derivedFrom":subQ18}),-1.0]])]})]);}
            var Q1;
            Q1=makeQuery(id+"F5.boolean.opBoolean","SPLIT",FACE,{"disambiguationData":[TD([makeQuery(id+"F5.opExtrude","SWEPT_FACE",FACE,{"disambiguationData":[OSD([sQuery(id+"F4.wireOp",EDGE,"E41")])]})])],"derivedFrom":makeQuery(id+"F3.boolean.opBoolean","COPY",FACE,{"derivedFrom":makeQuery(id+"F3.opExtrude","CAP_FACE",FACE,{"disambiguationData":[OSD([sQuery(id+"F0.wireOp",EDGE,"E25.0"),sQuery(id+"F0.wireOp",EDGE,"E25.1"),sQuery(id+"F0.wireOp",EDGE,"E25.2"),sQuery(id+"F0.wireOp",EDGE,"E25.3"),sQuery(id+"F0.wireOp",EDGE,"E25.4"),sQuery(id+"F0.wireOp",EDGE,"E25.5"),sQuery(id+"F0.wireOp",EDGE,"E25.6"),sQuery(id+"F0.wireOp",EDGE,"E25.7")])],"isStart":false})})});
            extrude(context, id + "F13", {"entities" : qUnion([Q0]), "operationType" : NewBodyOperationType.REMOVE, "endBound" : BoundingType.UP_TO_SURFACE, "endBoundEntityFace" : qUnion([Q1]), "depth" : 25 * mm});
        }
        {
            var Q0;
            Q0=makeQuery(id+"F3.boolean.opBoolean","COPY",EDGE,{"derivedFrom":makeQuery(id+"F3.opExtrude","CAP_EDGE",EDGE,{"disambiguationData":[OSD([sQuery(id+"F0.wireOp",EDGE,"E25.6")])],"isStart":false})});
            var Q1;
            Q1=makeQuery(id+"F8.boolean.opBoolean","INTERSECT",EDGE,{"derivedFrom":[makeQuery(id+"F5.opExtrude","SWEPT_FACE",FACE,{"disambiguationData":[OSD([sQuery(id+"F4.wireOp",EDGE,"E30")])]}),makeQuery(id+"F8.opExtrude","CAP_FACE",FACE,{"disambiguationData":[OSD([sQuery(id+"F7.wireOp",EDGE,"E67")])],"isStart":false})]});
            var Q2;
            Q2=makeQuery(id+"F8.boolean.opBoolean","INTERSECT",EDGE,{"disambiguationData":[OD(1.0)],"derivedFrom":[makeQuery(id+"F5.opExtrude","SWEPT_FACE",FACE,{"disambiguationData":[OSD([sQuery(id+"F4.wireOp",EDGE,"E30")])]}),makeQuery(id+"F8.opExtrude","SWEPT_FACE",FACE,{"disambiguationData":[OSD([sQuery(id+"F7.wireOp",EDGE,"E67")])]})]});
            var Q3;
            {var subQ0=sQuery(id+"F4.wireOp",EDGE,"E30");Q3=makeQuery(id+"F8.boolean.opBoolean","SPLIT",EDGE,{"disambiguationData":[TD([makeQuery(id+"F5.opExtrude","SWEPT_FACE",FACE,{"disambiguationData":[OSD([sQuery(id+"F4.wireOp",EDGE,"E35.filletArc")])]})])],"derivedFrom":makeQuery(id+"F5.opExtrude","CAP_EDGE",EDGE,{"disambiguationData":[OSD([subQ0])],"isStart":false})});}
            var Q4;
            {var subQ0=sQuery(id+"F0.wireOp",EDGE,"E25.7");var subQ1=sQuery(id+"F0.wireOp",EDGE,"E25.1");var subQ2=sQuery(id+"F0.wireOp",EDGE,"E25.6");var subQ3=sQuery(id+"F0.wireOp",EDGE,"E25.5");var subQ4=sQuery(id+"F0.wireOp",EDGE,"E25.4");var subQ5=sQuery(id+"F0.wireOp",EDGE,"E25.0");var subQ6=sQuery(id+"F0.wireOp",EDGE,"E25.2");var subQ7=sQuery(id+"F0.wireOp",EDGE,"E25.3");Q4=makeQuery(id+"F8.boolean.opBoolean","INTERSECT",EDGE,{"derivedFrom":[makeQuery(id+"F5.boolean.opBoolean","SPLIT",FACE,{"disambiguationData":[TD([makeQuery(id+"F2.opExtrude","SWEPT_FACE",FACE,{"disambiguationData":[OSD([subQ5])]})])],"derivedFrom":makeQuery(id+"F3.boolean.opBoolean","COPY",FACE,{"derivedFrom":makeQuery(id+"F3.opExtrude","CAP_FACE",FACE,{"disambiguationData":[OSD([subQ5,subQ1,subQ6,subQ7,subQ4,subQ3,subQ2,subQ0])],"isStart":false})})}),makeQuery(id+"F8.opExtrude","SWEPT_FACE",FACE,{"disambiguationData":[OSD([sQuery(id+"F7.wireOp",EDGE,"E67")])]})]});}
            var Q5;
            Q5=makeQuery(id+"F8.boolean.opBoolean","INTERSECT",EDGE,{"disambiguationData":[OD(0.0)],"derivedFrom":[makeQuery(id+"F5.opExtrude","SWEPT_FACE",FACE,{"disambiguationData":[OSD([sQuery(id+"F4.wireOp",EDGE,"E30")])]}),makeQuery(id+"F8.opExtrude","SWEPT_FACE",FACE,{"disambiguationData":[OSD([sQuery(id+"F7.wireOp",EDGE,"E67")])]})]});
            fillet(context, id + "F14", {"entities" : qUnion([Q0, Q1, Q2, Q3, Q4, Q5]), "radius" : 3 * mm, "tangentPropagation" : true, "allowEdgeOverflow" : false});
        }
        {
            var Q0;
            Q0=makeQuery(id+"F1.opExtrude","CAP_EDGE",EDGE,{"disambiguationData":[OSD([sQuery(id+"F0.wireOp",EDGE,"E1.bottom")])],"isStart":false});
            fillet(context, id + "F15", {"entities" : qUnion([Q0]), "radius" : 2 * mm, "tangentPropagation" : true, "allowEdgeOverflow" : false});
        }
        {
            var Q0;
            {var subQ0=sQuery(id+"F0.wireOp",EDGE,"E21.filletArc");var subQ1=sQuery(id+"F0.wireOp",EDGE,"E7");var subQ2=sQuery(id+"F0.wireOp",EDGE,"E6");var subQ3=sQuery(id+"F0.wireOp",EDGE,"E5");var subQ4=sQuery(id+"F0.wireOp",EDGE,"E4");var subQ5=sQuery(id+"F0.wireOp",EDGE,"E22.filletArc");var subQ6=sQuery(id+"F0.wireOp",EDGE,"E1.bottom");var subQ7=sQuery(id+"F0.wireOp",EDGE,"E1.right");var subQ8=sQuery(id+"F0.wireOp",EDGE,"E1.top");var subQ9=sQuery(id+"F0.wireOp",EDGE,"E1.left");var subQ10=sQuery(id+"F0.wireOp",EDGE,"E23.filletArc");var subQ11=sQuery(id+"F0.wireOp",EDGE,"E24.filletArc");Q0=makeQuery(id+"F2.boolean.opBoolean","SPLIT",FACE,{"disambiguationData":[TD([makeQuery(id+"F1.opExtrude","SWEPT_FACE",FACE,{"disambiguationData":[OSD([subQ6])]})])],"derivedFrom":makeQuery(id+"F1.opExtrude","CAP_FACE",FACE,{"disambiguationData":[OSD([subQ6,subQ8,subQ9,subQ7,subQ4,subQ3,subQ2,subQ1,subQ0,subQ5,subQ10,subQ11])],"isStart":true})});}
            var sketch = newSketch(context, id + "F16", { "sketchPlane" : qUnion([Q0])});
            skCircle(sketch, "E79", {"center": v(0, 104.25) * mm, "radius": 6 * mm});
            skArc(sketch, "E80", {"start": v(15, 104.25) * mm, "mid": v(0, 119.25) * mm, "end": v(-15, 104.25) * mm});
            skLineSegment(sketch, "E81", {"start": v(-15, 104.25) * mm, "end": v(-15, 92.25) * mm});
            skLineSegment(sketch, "E82", {"start": v(15, 104.25) * mm, "end": v(15, 92.25) * mm});
            skLineSegment(sketch, "E83", {"start": v(15, 92.25) * mm, "end": v(33, 74.25) * mm});
            skLineSegment(sketch, "E84", {"start": v(-15, 92.25) * mm, "end": v(-33, 74.25) * mm});
            skLineSegment(sketch, "E85", {"start": v(60, 0) * mm, "end": v(-60, 0) * mm});
            skLineSegment(sketch, "E86.MirrorCS", {"start": v(-15, -104.25) * mm, "end": v(-15, -92.25) * mm});
            skArc(sketch, "E87.MirrorCS", {"start": v(15, -104.25) * mm, "mid": v(0, -119.25) * mm, "end": v(-15, -104.25) * mm});
            skLineSegment(sketch, "E88.MirrorCS", {"start": v(-15, -92.25) * mm, "end": v(-33, -74.25) * mm});
            skLineSegment(sketch, "E89.MirrorCS", {"start": v(15, -104.25) * mm, "end": v(15, -92.25) * mm});
            skLineSegment(sketch, "E90.MirrorCS", {"start": v(15, -92.25) * mm, "end": v(33, -74.25) * mm});
            skCircle(sketch, "E91", {"center": v(0, -104.25) * mm, "radius": 6 * mm});
            skSolve(sketch);
        }
        {
            var Q0;
            Q0 = qSketchRegion(id + "F16", true);
            var Q1;
            {var subQ3=sQuery(id+"F16.wireOp",EDGE,"E88.MirrorCS");Q1=makeQuery(id+"F16.imprint","IMPRINT",FACE,{"disambiguationData":[TD([[makeQuery(id+"F16.imprint","IMPRINT",EDGE,{"derivedFrom":subQ3}),-1.0]])]});}
            var Q2;
            Q2=makeQuery(id+"F16.imprint","IMPRINT",FACE,{"disambiguationData":[TD([[makeQuery(id+"F16.imprint","IMPRINT",EDGE,{"derivedFrom":sQuery(id+"F16.wireOp",EDGE,"E79")}),-1.0]])]});
            var Q3;
            Q3=makeQuery(id+"F16.imprint","IMPRINT",FACE,{"disambiguationData":[TD([[makeQuery(id+"F16.imprint","IMPRINT",EDGE,{"derivedFrom":makeQuery(id+"F1.opExtrude","CAP_EDGE",EDGE,{"disambiguationData":[OSD([sQuery(id+"F0.wireOp",EDGE,"E1.left")])],"isStart":true})}),-1.0]])]});
            extrude(context, id + "F17", {"entities" : qUnion([Q0, Q1, Q2, Q3]), "operationType" : NewBodyOperationType.ADD, "depth" : 25 * mm});
        }
        {
            var Q0;
            Q0 = qSketchRegion(id + "F16", true);
            extrude(context, id + "F18", {"entities" : qUnion([Q0]), "operationType" : NewBodyOperationType.ADD, "depth" : 25 * mm});
        }
    });
